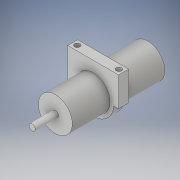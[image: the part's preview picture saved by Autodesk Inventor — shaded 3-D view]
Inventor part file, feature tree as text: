
AUTODESK INVENTOR PART (.ipt)
format: ipt  version: 2019 (Build 230136000, 136)  size: 145,920 bytes
history: native  units: in
note: dims shown in document units (in); Inventor stores cm internally (conversion verified against a paired STEP export)
features: extrude x4, sketch x4, plane x1
ambient origin geometry x8: Origin, YZ Plane, XZ Plane, XY Plane, X Axis, Y Axis, Z Axis, Center Point
bodies: Solid1 (feature_tree)
feature tree (9):
  extrude  "Extrusion1"  Depth=2.3622in TaperAngle=0.0deg
  extrude  "Extrusion2"  Depth=0.5906in TaperAngle=0.0deg
  plane  "Work Plane1"
  extrude  "Extrusion3"  Depth=1.2992in
  extrude  "Extrusion4"  Depth=0.1969in
  sketch  "Sketch1"  dims[d0=0.8661in d1=2.3622in d2=0.0in]
  sketch  "Sketch2"  dims[d3=0.1575in d4=0.5906in d5=0.0in]
  sketch  "Sketch3"  dims[d6=-1.1417in d7=1.2992in]
  sketch  "Sketch4"  dims[d8=1.4173in d9=1.063in d10=1.063in d11=0.748in d12=0.2559in d13=0.0in d14=1.2992in d15=0.128in d16=0.1181in d17=0.1181in d18=0.1378in d19=0.1378in d20=0.1969in d21=0.0in]
